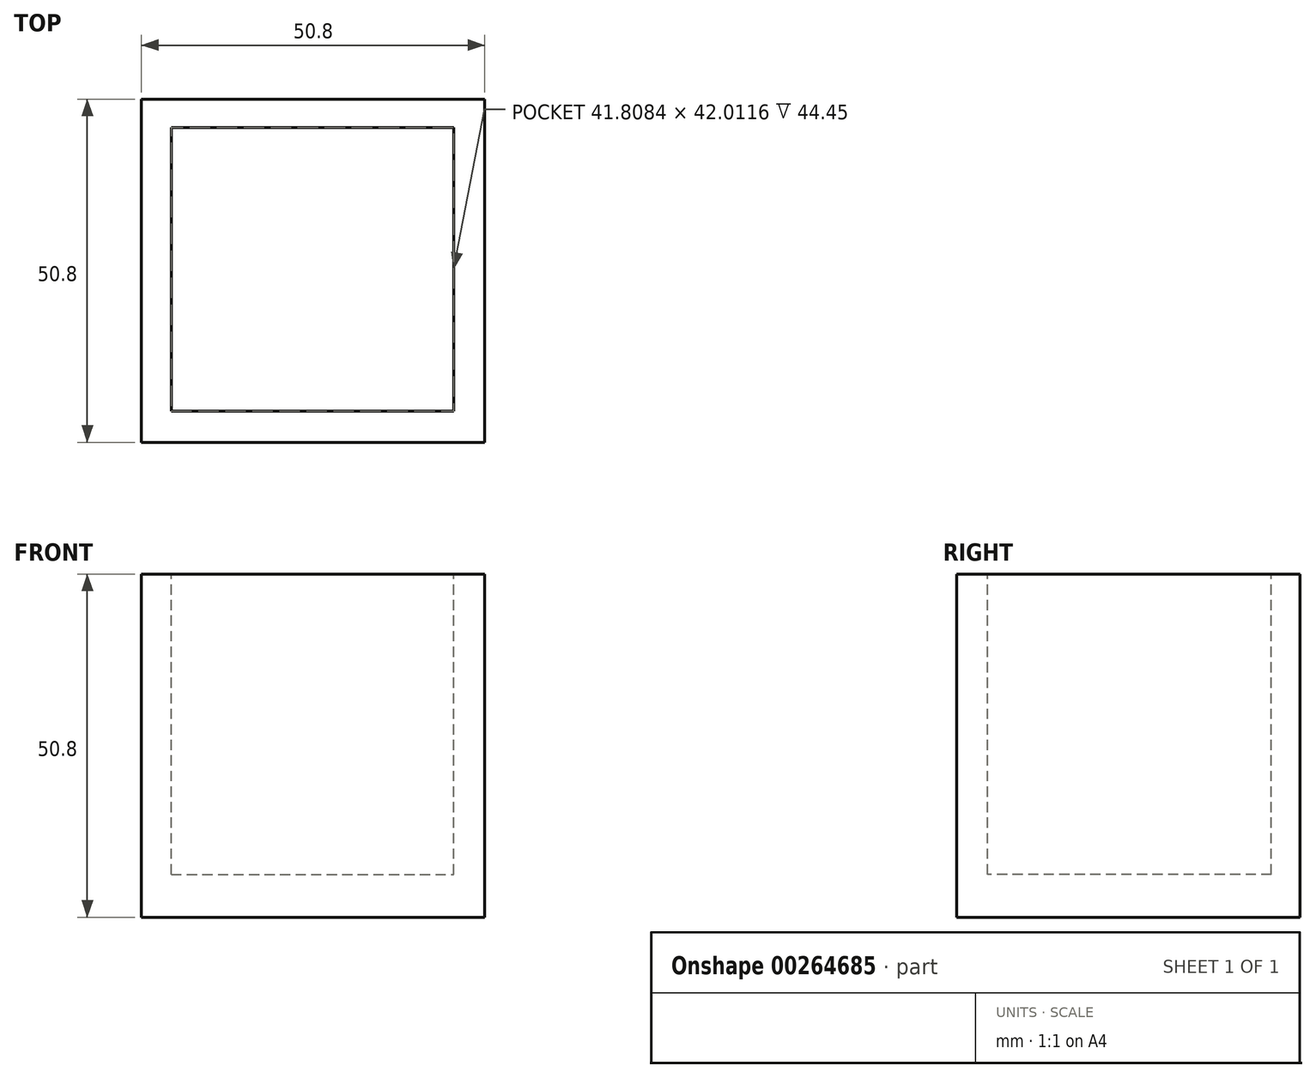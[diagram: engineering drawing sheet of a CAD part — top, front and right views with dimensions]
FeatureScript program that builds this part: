
annotation { "Feature Type Name" : "Feature", "Feature Type Description" : "" }
export const myFeature = defineFeature(function(context is Context, id is Id, definition is map)
    precondition{}
    {
        {
            var Q0;
            Q0=qCreatedBy(makeId("Front.planeOp"),FACE);
            var sketch = newSketch(context, id + "F0", { "sketchPlane" : qUnion([Q0])});
            skLineSegment(sketch, "E0.bottom", {"start": v(0, 0) * mm, "end": v(-50.8, 0) * mm});
            skLineSegment(sketch, "E0.top", {"start": v(0, 50.8) * mm, "end": v(-50.8, 50.8) * mm});
            skLineSegment(sketch, "E0.left", {"start": v(0, 0) * mm, "end": v(0, 50.8) * mm});
            skLineSegment(sketch, "E0.right", {"start": v(-50.8, 0) * mm, "end": v(-50.8, 50.8) * mm});
            skSolve(sketch);
        }
        {
            var Q0;
            Q0 = qSketchRegion(id + "F0", true);
            extrude(context, id + "F1", {"entities" : qUnion([Q0]), "depth" : 50.8 * mm});
        }
        {
            var Q0;
            Q0=makeQuery(id+"F1.opExtrude","SWEPT_FACE",FACE,{"disambiguationData":[OSD([sQuery(id+"F0.wireOp",EDGE,"E0.top")])]});
            var sketch = newSketch(context, id + "F2", { "sketchPlane" : qUnion([Q0])});
            skLineSegment(sketch, "E1.bottom", {"start": v(-46.4, -4.2) * mm, "end": v(-4.58, -4.2) * mm});
            skLineSegment(sketch, "E1.top", {"start": v(-46.4, -46.21) * mm, "end": v(-4.58, -46.21) * mm});
            skLineSegment(sketch, "E1.left", {"start": v(-46.4, -4.2) * mm, "end": v(-46.4, -46.21) * mm});
            skLineSegment(sketch, "E1.right", {"start": v(-4.58, -4.2) * mm, "end": v(-4.58, -46.21) * mm});
            skSolve(sketch);
        }
        {
            var Q0;
            Q0=makeQuery(id+"F2.imprint","IMPRINT",FACE,{"disambiguationData":[TD([[makeQuery(id+"F2.imprint","IMPRINT",EDGE,{"derivedFrom":sQuery(id+"F2.wireOp",EDGE,"E1.bottom")}),-1.0]])]});
            extrude(context, id + "F3", {"entities" : qUnion([Q0]), "operationType" : NewBodyOperationType.REMOVE, "oppositeDirection" : true, "depth" : 44.45 * mm});
        }
    });
